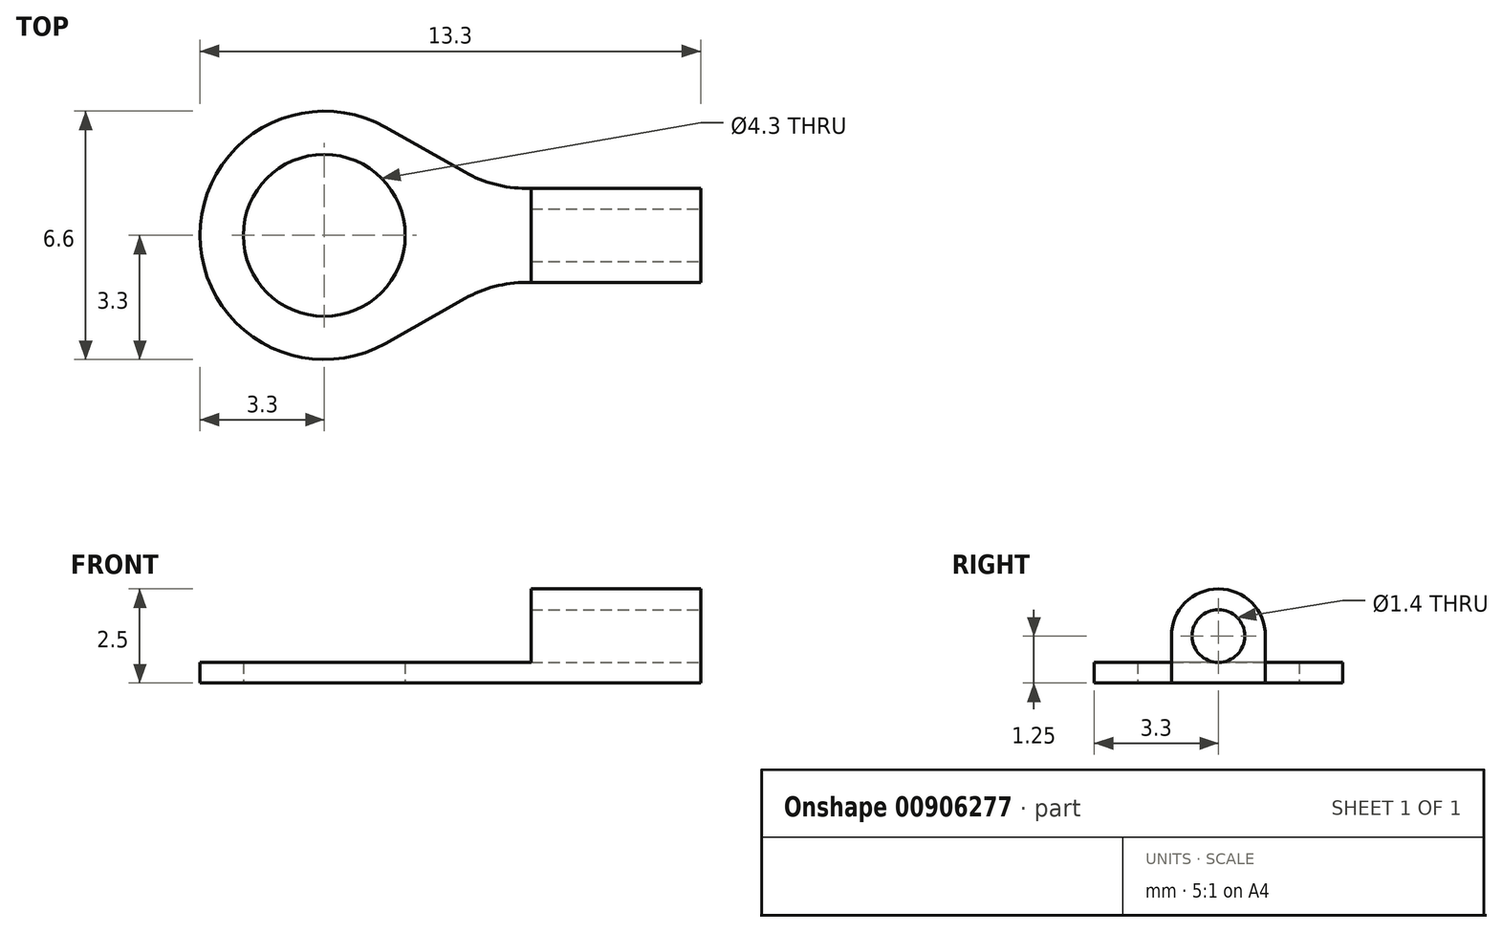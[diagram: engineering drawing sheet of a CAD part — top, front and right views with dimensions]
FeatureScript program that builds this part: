
annotation { "Feature Type Name" : "Feature", "Feature Type Description" : "" }
export const myFeature = defineFeature(function(context is Context, id is Id, definition is map)
    precondition{}
    {
        {
            var Q0;
            Q0=qCreatedBy(makeId("Top.planeOp"),FACE);
            var sketch = newSketch(context, id + "F0", { "sketchPlane" : qUnion([Q0])});
            skLineSegment(sketch, "E0", {"start": v(13.3, 2.05) * mm, "end": v(13.3, 4.55) * mm});
            skLineSegment(sketch, "E1", {"start": v(0, 3.3) * mm, "end": v(0, 3.3) * mm});
            skPoint(sketch, "E2.visualSharp", {"position": v(0, 6.6) * mm});
            skArc(sketch, "E2.filletArc", {"start": v(3.3, 6.6) * mm, "mid": v(0.97, 5.63) * mm, "end": v(0, 3.3) * mm});
            skPoint(sketch, "E3.visualSharp", {"position": v(0, 0) * mm});
            skArc(sketch, "E3.filletArc", {"start": v(0, 3.3) * mm, "mid": v(0.97, 0.97) * mm, "end": v(3.3, 0) * mm});
            skLineSegment(sketch, "E4.0", {"start": v(13.3, 4.55) * mm, "end": v(8.67, 4.55) * mm});
            skLineSegment(sketch, "E5.0", {"start": v(13.3, 2.05) * mm, "end": v(8.67, 2.05) * mm});
            skCircle(sketch, "E6", {"center": v(3.3, 3.3) * mm, "radius": 2.15 * mm});
            skArc(sketch, "E7", {"start": v(4.92, 6.17) * mm, "mid": v(0, 3.3) * mm, "end": v(4.92, 0.43) * mm});
            skLineSegment(sketch, "E8", {"start": v(7.05, 4.98) * mm, "end": v(4.92, 6.17) * mm});
            skLineSegment(sketch, "E9", {"start": v(7.05, 1.62) * mm, "end": v(4.92, 0.43) * mm});
            skPoint(sketch, "E10.visualSharp", {"position": v(7.8, 4.55) * mm});
            skArc(sketch, "E10.filletArc", {"start": v(7.05, 4.98) * mm, "mid": v(7.83, 4.66) * mm, "end": v(8.67, 4.55) * mm});
            skPoint(sketch, "E11.visualSharp", {"position": v(7.8, 2.05) * mm});
            skArc(sketch, "E11.filletArc", {"start": v(8.67, 2.05) * mm, "mid": v(7.83, 1.94) * mm, "end": v(7.05, 1.62) * mm});
            skPoint(sketch, "E12.orphan", {"position": v(13.3, 6.6) * mm});
            skPoint(sketch, "E13.orphan", {"position": v(7.8, 6.6) * mm});
            skPoint(sketch, "E14.orphan", {"position": v(13.3, 0) * mm});
            skPoint(sketch, "E15.end.orphan", {"position": v(7.8, 0) * mm});
            skPoint(sketch, "E16.end.orphan", {"position": v(7.8, 3.3) * mm});
            skPoint(sketch, "E16.start.orphan", {"position": v(13.3, 3.3) * mm});
            skSolve(sketch);
        }
        {
            var Q0;
            Q0 = qSketchRegion(id + "F0", true);
            extrude(context, id + "F1", {"entities" : qUnion([Q0]), "depth" : 0.55 * mm, "offsetDistance" : 25 * mm});
        }
        {
            var Q0;
            Q0=makeQuery(id+"F1.opExtrude","CAP_FACE",FACE,{"disambiguationData":[OSD([sQuery(id+"F0.wireOp",EDGE,"E0"),sQuery(id+"F0.wireOp",EDGE,"E4.0"),sQuery(id+"F0.wireOp",EDGE,"E5.0"),sQuery(id+"F0.wireOp",EDGE,"E6"),sQuery(id+"F0.wireOp",EDGE,"E7"),sQuery(id+"F0.wireOp",EDGE,"E8"),sQuery(id+"F0.wireOp",EDGE,"E9"),sQuery(id+"F0.wireOp",EDGE,"E10.filletArc"),sQuery(id+"F0.wireOp",EDGE,"E11.filletArc")])],"isStart":false});
            var sketch = newSketch(context, id + "F2", { "sketchPlane" : qUnion([Q0])});
            skLineSegment(sketch, "E17.bottom", {"start": v(13.3, 4.55) * mm, "end": v(8.8, 4.55) * mm});
            skLineSegment(sketch, "E17.top", {"start": v(13.3, 2.05) * mm, "end": v(8.8, 2.05) * mm});
            skLineSegment(sketch, "E17.left", {"start": v(13.3, 4.55) * mm, "end": v(13.3, 2.05) * mm});
            skLineSegment(sketch, "E17.right", {"start": v(8.8, 4.55) * mm, "end": v(8.8, 2.05) * mm});
            skSolve(sketch);
        }
        {
            var Q0;
            Q0 = qSketchRegion(id + "F2", true);
            extrude(context, id + "F3", {"entities" : qUnion([Q0]), "operationType" : NewBodyOperationType.ADD, "depth" : 1.95 * mm, "offsetDistance" : 25 * mm});
        }
        {
            var Q0;
            Q0=makeQuery(id+"F3.opExtrude","CAP_EDGE",EDGE,{"disambiguationData":[OSD([sQuery(id+"F2.wireOp",EDGE,"E17.bottom")])],"isStart":false});
            var Q1;
            Q1=makeQuery(id+"F3.opExtrude","CAP_EDGE",EDGE,{"disambiguationData":[OSD([sQuery(id+"F2.wireOp",EDGE,"E17.top")])],"isStart":false});
            fillet(context, id + "F4", {"entities" : qUnion([Q0, Q1]), "radius" : 1.25 * mm, "tangentPropagation" : true, "allowEdgeOverflow" : false});
        }
        {
            var Q0;
            Q0=makeQuery(id+"F3.boolean.opBoolean","MERGE",FACE,{"derivedFrom":[makeQuery(id+"F1.opExtrude","SWEPT_FACE",FACE,{"disambiguationData":[OSD([sQuery(id+"F0.wireOp",EDGE,"E0")])]}),makeQuery(id+"F3.opExtrude","SWEPT_FACE",FACE,{"disambiguationData":[OSD([sQuery(id+"F2.wireOp",EDGE,"E17.left")])]})]});
            var sketch = newSketch(context, id + "F5", { "sketchPlane" : qUnion([Q0])});
            skCircle(sketch, "E18", {"center": v(3.3, 1.25) * mm, "radius": 0.7 * mm});
            skSolve(sketch);
        }
        {
            var Q0;
            Q0 = qSketchRegion(id + "F5", true);
            extrude(context, id + "F6", {"entities" : qUnion([Q0]), "operationType" : NewBodyOperationType.REMOVE, "oppositeDirection" : true, "depth" : 25 * mm, "offsetDistance" : 25 * mm});
        }
    });
